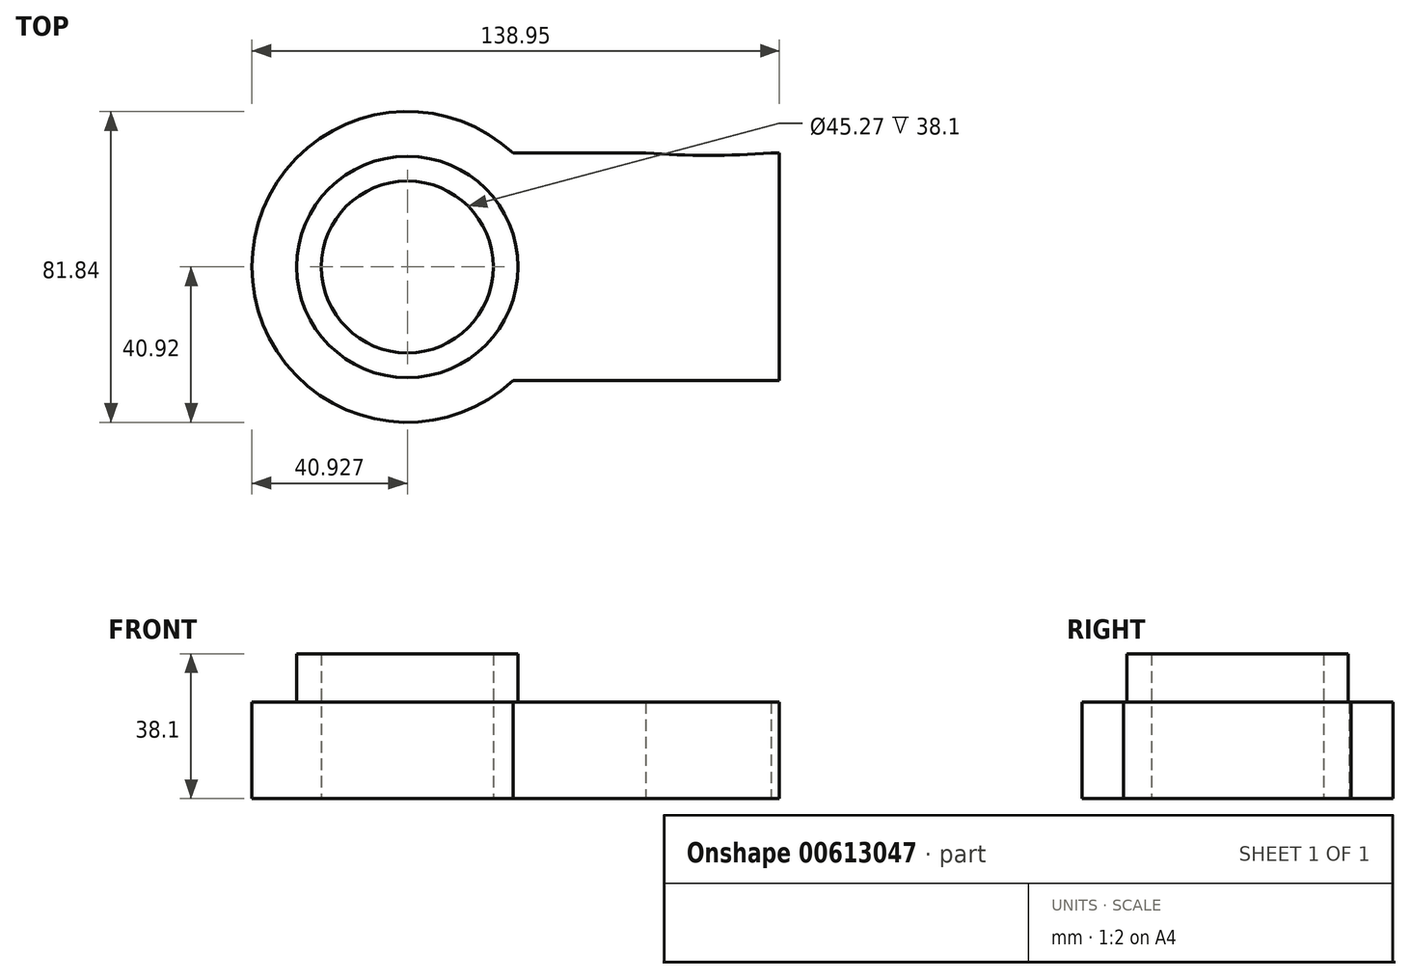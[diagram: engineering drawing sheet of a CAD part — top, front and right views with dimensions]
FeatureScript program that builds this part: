
annotation { "Feature Type Name" : "Feature", "Feature Type Description" : "" }
export const myFeature = defineFeature(function(context is Context, id is Id, definition is map)
    precondition{}
    {
        {
            var Q0;
            Q0=qCreatedBy(makeId("Top.planeOp"),FACE);
            var sketch = newSketch(context, id + "F0", { "sketchPlane" : qUnion([Q0])});
            skLineSegment(sketch, "E0.bottom", {"start": v(-49.01, 29.96) * mm, "end": v(49.01, 29.96) * mm});
            skLineSegment(sketch, "E0.top", {"start": v(-49.01, -29.96) * mm, "end": v(49.01, -29.96) * mm});
            skLineSegment(sketch, "E0.left", {"start": v(-49.01, 29.96) * mm, "end": v(-49.01, -29.96) * mm});
            skLineSegment(sketch, "E0.right", {"start": v(49.01, 29.96) * mm, "end": v(49.01, -29.96) * mm});
            skPoint(sketch, "E0.middle", {"position": v(0, 0) * mm});
            skCircle(sketch, "E1", {"center": v(-49.01, 0) * mm, "radius": 22.64 * mm});
            skCircle(sketch, "E2", {"center": v(-49.01, 0) * mm, "radius": 40.92 * mm});
            skCircle(sketch, "E3", {"center": v(-49.01, 0) * mm, "radius": 29.14 * mm});
            skArc(sketch, "E4", {"start": v(-37.36, 39.23) * mm, "mid": v(4.3, 30.82) * mm, "end": v(46.77, 29.96) * mm});
            skSolve(sketch);
        }
        {
            var Q0;
            {var subQ0=sQuery(id+"F0.wireOp",EDGE,"E0.right");Q0=makeQuery(id+"F0.imprint","IMPRINT",FACE,{"disambiguationData":[TD([[makeQuery(id+"F0.imprint","IMPRINT",EDGE,{"derivedFrom":subQ0}),-1.0]])]});}
            var Q1;
            {var subQ0=sQuery(id+"F0.wireOp",EDGE,"E0.left");var subQ1=sQuery(id+"F0.wireOp",EDGE,"E0.bottom");var subQ2=makeQuery(id+"F0.imprint","INTERSECT",VERTEX,{"derivedFrom":[subQ1,subQ0]});Q1=makeQuery(id+"F0.imprint","IMPRINT",FACE,{"disambiguationData":[TD([[makeQuery(id+"F0.imprint","IMPRINT",EDGE,{"disambiguationData":[TD([[subQ2,-1.0]])],"derivedFrom":subQ1}),1.0]])]});}
            var Q2;
            {var subQ0=sQuery(id+"F0.wireOp",EDGE,"E0.left");var subQ1=sQuery(id+"F0.wireOp",EDGE,"E0.bottom");var subQ2=makeQuery(id+"F0.imprint","INTERSECT",VERTEX,{"derivedFrom":[subQ1,subQ0]});Q2=makeQuery(id+"F0.imprint","IMPRINT",FACE,{"disambiguationData":[TD([[makeQuery(id+"F0.imprint","IMPRINT",EDGE,{"disambiguationData":[TD([[subQ2,-1.0]])],"derivedFrom":subQ1}),-1.0]])]});}
            extrude(context, id + "F1", {"entities" : qUnion([Q0, Q1, Q2]), "depth" : 25.4 * mm, "offsetDistance" : 25.4 * mm});
        }
        {
            var Q0;
            {var subQ0=sQuery(id+"F0.wireOp",EDGE,"E3");var subQ1=sQuery(id+"F0.wireOp",EDGE,"E0.left");var subQ2=makeQuery(id+"F0.imprint","INTERSECT",VERTEX,{"disambiguationData":[OD(0.0)],"derivedFrom":[subQ1,subQ0]});Q0=makeQuery(id+"F0.imprint","IMPRINT",FACE,{"disambiguationData":[TD([[makeQuery(id+"F0.imprint","IMPRINT",EDGE,{"disambiguationData":[TD([[subQ2,-1.0]])],"derivedFrom":subQ1}),1.0]])]});}
            var Q1;
            {var subQ0=sQuery(id+"F0.wireOp",EDGE,"E3");var subQ1=sQuery(id+"F0.wireOp",EDGE,"E0.left");var subQ2=makeQuery(id+"F0.imprint","INTERSECT",VERTEX,{"disambiguationData":[OD(0.0)],"derivedFrom":[subQ1,subQ0]});Q1=makeQuery(id+"F0.imprint","IMPRINT",FACE,{"disambiguationData":[TD([[makeQuery(id+"F0.imprint","IMPRINT",EDGE,{"disambiguationData":[TD([[subQ2,-1.0]])],"derivedFrom":subQ1}),-1.0]])]});}
            extrude(context, id + "F2", {"entities" : qUnion([Q0, Q1]), "operationType" : NewBodyOperationType.ADD, "depth" : 38.1 * mm, "offsetDistance" : 25.4 * mm});
        }
    });
